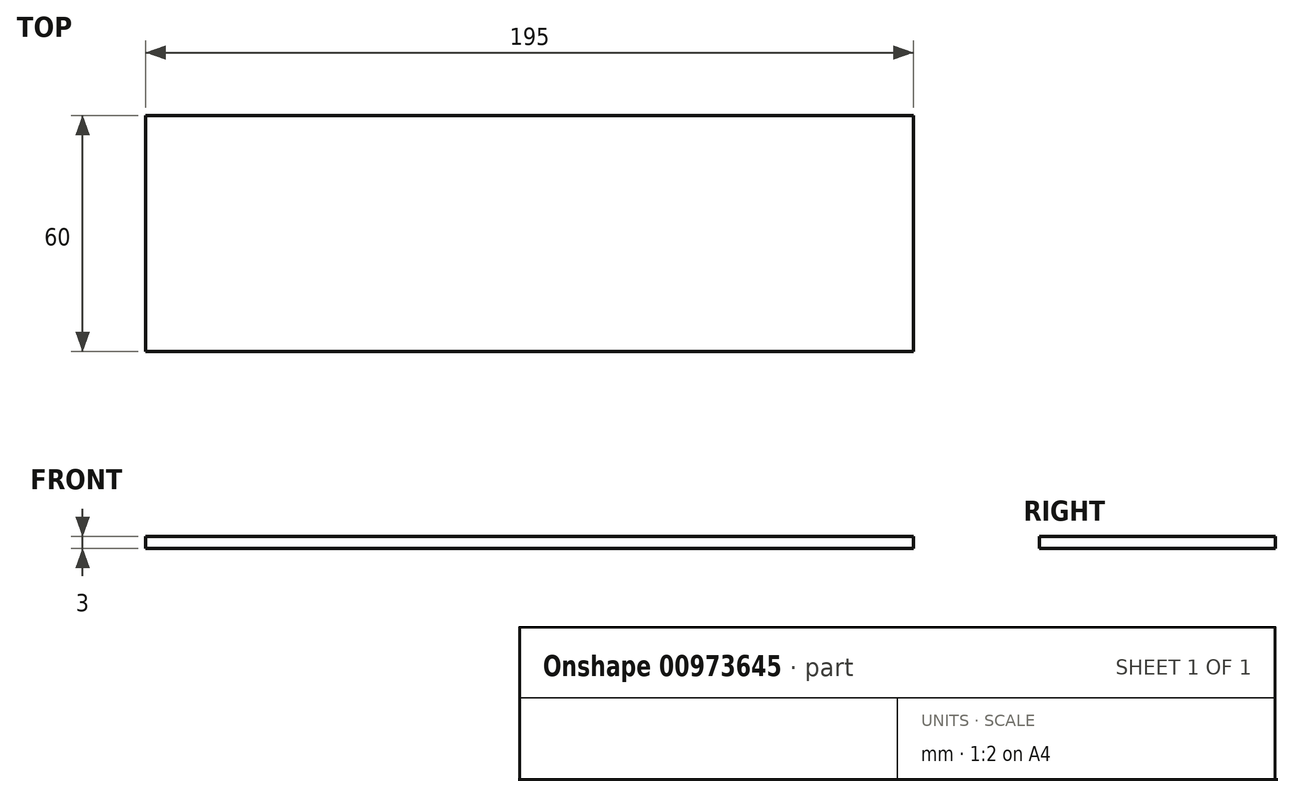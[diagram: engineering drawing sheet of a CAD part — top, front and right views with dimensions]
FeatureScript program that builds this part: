
annotation { "Feature Type Name" : "Feature", "Feature Type Description" : "" }
export const myFeature = defineFeature(function(context is Context, id is Id, definition is map)
    precondition{}
    {
        {
            var Q0;
            Q0=qCreatedBy(makeId("Top.planeOp"),FACE);
            var sketch = newSketch(context, id + "F0", { "sketchPlane" : qUnion([Q0])});
            skLineSegment(sketch, "E0", {"start": v(0, 0) * mm, "end": v(195, 0) * mm});
            skLineSegment(sketch, "E1", {"start": v(195, 0) * mm, "end": v(195, -60) * mm});
            skLineSegment(sketch, "E2", {"start": v(195, -60) * mm, "end": v(0, -60) * mm});
            skLineSegment(sketch, "E3", {"start": v(0, -60) * mm, "end": v(0, 0) * mm});
            skSolve(sketch);
        }
        {
            var Q0;
            Q0=makeQuery(id+"F0.imprint","IMPRINT",FACE,{"disambiguationData":[TD([[makeQuery(id+"F0.imprint","IMPRINT",EDGE,{"derivedFrom":sQuery(id+"F0.wireOp",EDGE,"E0")}),-1.0]])]});
            extrude(context, id + "F1", {"entities" : qUnion([Q0]), "depth" : 3 * mm, "offsetDistance" : 25 * mm});
        }
    });
